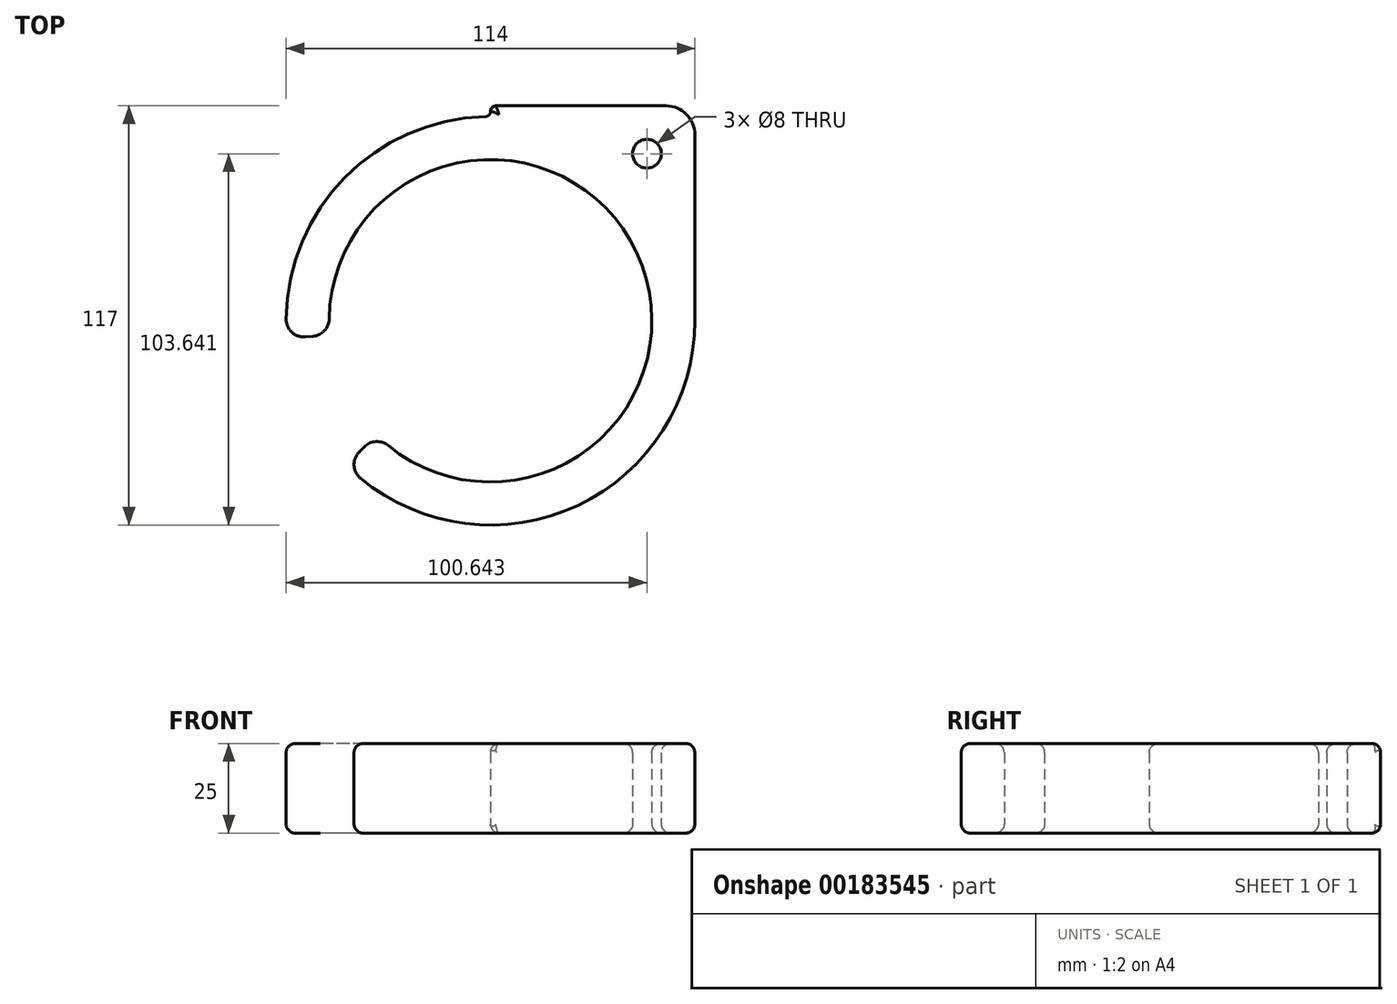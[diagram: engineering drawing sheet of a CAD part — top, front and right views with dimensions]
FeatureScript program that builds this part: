
annotation { "Feature Type Name" : "Feature", "Feature Type Description" : "" }
export const myFeature = defineFeature(function(context is Context, id is Id, definition is map)
    precondition{}
    {
        {
            var Q0;
            Q0=qCreatedBy(makeId("Top.planeOp"),FACE);
            var sketch = newSketch(context, id + "F0", { "sketchPlane" : qUnion([Q0])});
            skCircle(sketch, "E0", {"center": v(-22.2, -19.05) * mm, "radius": 45 * mm});
            skCircle(sketch, "E1", {"center": v(-22.2, -19.05) * mm, "radius": 57 * mm});
            skLineSegment(sketch, "E2.bottom", {"start": v(-22.2, -19.05) * mm, "end": v(34.8, -19.05) * mm});
            skLineSegment(sketch, "E2.top", {"start": v(-22.2, 40.95) * mm, "end": v(34.8, 40.95) * mm});
            skLineSegment(sketch, "E2.left", {"start": v(-22.2, -19.05) * mm, "end": v(-22.2, 40.95) * mm});
            skLineSegment(sketch, "E2.right", {"start": v(34.8, -19.05) * mm, "end": v(34.8, 40.95) * mm});
            skLineSegment(sketch, "E3", {"start": v(34.8, 40.95) * mm, "end": v(8.08, 14.23) * mm, "construction": true});
            skCircle(sketch, "E4", {"center": v(21.43, 27.6) * mm, "radius": 4 * mm});
            skLineSegment(sketch, "E5", {"start": v(-22.2, -19.05) * mm, "end": v(-79, -24.02) * mm});
            skLineSegment(sketch, "E6", {"start": v(-22.2, -19.05) * mm, "end": v(-62.51, -59.36) * mm});
            skSolve(sketch);
        }
        {
            var Q0;
            {var subQ0=sQuery(id+"F0.wireOp",EDGE,"E2.left");var subQ1=sQuery(id+"F0.wireOp",EDGE,"E0");var subQ2=makeQuery(id+"F0.imprint","INTERSECT",VERTEX,{"derivedFrom":[subQ1,subQ0]});Q0=makeQuery(id+"F0.imprint","IMPRINT",FACE,{"disambiguationData":[TD([[makeQuery(id+"F0.imprint","IMPRINT",EDGE,{"disambiguationData":[TD([[subQ2,1.0]])],"derivedFrom":subQ1}),-1.0]])]});}
            var Q1;
            {var subQ2=sQuery(id+"F0.wireOp",EDGE,"E2.top");Q1=makeQuery(id+"F0.imprint","IMPRINT",FACE,{"disambiguationData":[TD([[makeQuery(id+"F0.imprint","IMPRINT",EDGE,{"derivedFrom":subQ2}),-1.0]])]});}
            var Q2;
            {var subQ0=sQuery(id+"F0.wireOp",EDGE,"E2.left");var subQ1=sQuery(id+"F0.wireOp",EDGE,"E0");var subQ2=makeQuery(id+"F0.imprint","INTERSECT",VERTEX,{"derivedFrom":[subQ1,subQ0]});Q2=makeQuery(id+"F0.imprint","IMPRINT",FACE,{"disambiguationData":[TD([[makeQuery(id+"F0.imprint","IMPRINT",EDGE,{"disambiguationData":[TD([[subQ2,-1.0]])],"derivedFrom":subQ1}),-1.0]])]});}
            var Q3;
            {var subQ0=sQuery(id+"F0.wireOp",EDGE,"E2.bottom");var subQ1=sQuery(id+"F0.wireOp",EDGE,"E0");var subQ2=makeQuery(id+"F0.imprint","INTERSECT",VERTEX,{"derivedFrom":[subQ1,subQ0]});Q3=makeQuery(id+"F0.imprint","IMPRINT",FACE,{"disambiguationData":[TD([[makeQuery(id+"F0.imprint","IMPRINT",EDGE,{"disambiguationData":[TD([[subQ2,1.0]])],"derivedFrom":subQ1}),-1.0]])]});}
            extrude(context, id + "F1", {"entities" : qUnion([Q0, Q1, Q2, Q3]), "depth" : 25 * mm});
        }
        {
            var Q0;
            Q0=makeQuery(id+"F1.opExtrude","SWEPT_EDGE",EDGE,{"disambiguationData":[OSD([sQuery(id+"F0.wireOp",EDGE,"E2.top"),sQuery(id+"F0.wireOp",EDGE,"E2.left")])]});
            var Q1;
            Q1=makeQuery(id+"F1.opExtrude","SWEPT_EDGE",EDGE,{"disambiguationData":[OSD([sQuery(id+"F0.wireOp",EDGE,"E1"),sQuery(id+"F0.wireOp",EDGE,"E2.left")])]});
            fillet(context, id + "F2", {"entities" : qUnion([Q0, Q1]), "radius" : 1.5 * mm, "tangentPropagation" : true, "allowEdgeOverflow" : false});
        }
        {
            var Q0;
            Q0=makeQuery(id+"F1.opExtrude","SWEPT_EDGE",EDGE,{"disambiguationData":[OSD([sQuery(id+"F0.wireOp",EDGE,"E0"),sQuery(id+"F0.wireOp",EDGE,"E5")])]});
            var Q1;
            Q1=makeQuery(id+"F1.opExtrude","SWEPT_EDGE",EDGE,{"disambiguationData":[OSD([sQuery(id+"F0.wireOp",EDGE,"E0"),sQuery(id+"F0.wireOp",EDGE,"E6")])]});
            var Q2;
            Q2=makeQuery(id+"F1.opExtrude","SWEPT_EDGE",EDGE,{"disambiguationData":[OSD([sQuery(id+"F0.wireOp",EDGE,"E1"),sQuery(id+"F0.wireOp",EDGE,"E6")])]});
            var Q3;
            Q3=makeQuery(id+"F1.opExtrude","SWEPT_EDGE",EDGE,{"disambiguationData":[OSD([sQuery(id+"F0.wireOp",EDGE,"E1"),sQuery(id+"F0.wireOp",EDGE,"E5")])]});
            fillet(context, id + "F3", {"entities" : qUnion([Q0, Q1, Q2, Q3]), "radius" : 5 * mm, "tangentPropagation" : true, "allowEdgeOverflow" : false});
        }
        {
            var Q0;
            Q0=makeQuery(id+"F1.opExtrude","SWEPT_EDGE",EDGE,{"disambiguationData":[OSD([sQuery(id+"F0.wireOp",EDGE,"E2.top"),sQuery(id+"F0.wireOp",EDGE,"E2.right")])]});
            fillet(context, id + "F4", {"entities" : qUnion([Q0]), "radius" : 8 * mm, "tangentPropagation" : true, "allowEdgeOverflow" : false});
        }
        {
            var Q0;
            Q0=makeQuery(id+"F1.opExtrude","CAP_EDGE",EDGE,{"disambiguationData":[OSD([sQuery(id+"F0.wireOp",EDGE,"E0")])],"isStart":true});
            var Q1;
            {var subQ0=sQuery(id+"F0.wireOp",EDGE,"E5");var subQ1=sQuery(id+"F0.wireOp",EDGE,"E0");Q1=makeQuery(id+"F3.opFillet","BLEND_EDGE",EDGE,{"blendedFrom":[makeQuery(id+"F1.opExtrude","SWEPT_EDGE",EDGE,{"disambiguationData":[OSD([subQ1,subQ0])]}),makeQuery(id+"F1.opExtrude","CAP_FACE",FACE,{"disambiguationData":[OSD([subQ1,sQuery(id+"F0.wireOp",EDGE,"E1"),sQuery(id+"F0.wireOp",EDGE,"E2.top"),sQuery(id+"F0.wireOp",EDGE,"E2.left"),sQuery(id+"F0.wireOp",EDGE,"E2.right"),sQuery(id+"F0.wireOp",EDGE,"E4"),subQ0,sQuery(id+"F0.wireOp",EDGE,"E6")])],"isStart":true})],"blendedInto":[makeQuery(id+"F1.opExtrude","CAP_FACE",FACE,{"disambiguationData":[OSD([subQ1,sQuery(id+"F0.wireOp",EDGE,"E1"),sQuery(id+"F0.wireOp",EDGE,"E2.top"),sQuery(id+"F0.wireOp",EDGE,"E2.left"),sQuery(id+"F0.wireOp",EDGE,"E2.right"),sQuery(id+"F0.wireOp",EDGE,"E4"),subQ0,sQuery(id+"F0.wireOp",EDGE,"E6")])],"isStart":true})]});}
            var Q2;
            Q2=makeQuery(id+"F1.opExtrude","CAP_FACE",FACE,{"disambiguationData":[OSD([sQuery(id+"F0.wireOp",EDGE,"E0"),sQuery(id+"F0.wireOp",EDGE,"E1"),sQuery(id+"F0.wireOp",EDGE,"E2.top"),sQuery(id+"F0.wireOp",EDGE,"E2.left"),sQuery(id+"F0.wireOp",EDGE,"E2.right"),sQuery(id+"F0.wireOp",EDGE,"E4"),sQuery(id+"F0.wireOp",EDGE,"E5"),sQuery(id+"F0.wireOp",EDGE,"E6")])],"isStart":true});
            var Q3;
            Q3=makeQuery(id+"F1.opExtrude","CAP_FACE",FACE,{"disambiguationData":[OSD([sQuery(id+"F0.wireOp",EDGE,"E0"),sQuery(id+"F0.wireOp",EDGE,"E1"),sQuery(id+"F0.wireOp",EDGE,"E2.top"),sQuery(id+"F0.wireOp",EDGE,"E2.left"),sQuery(id+"F0.wireOp",EDGE,"E2.right"),sQuery(id+"F0.wireOp",EDGE,"E4"),sQuery(id+"F0.wireOp",EDGE,"E5"),sQuery(id+"F0.wireOp",EDGE,"E6")])],"isStart":false});
            fillet(context, id + "F5", {"entities" : qUnion([Q0, Q1, Q2, Q3]), "radius" : 2.5 * mm, "tangentPropagation" : true, "allowEdgeOverflow" : false});
        }
    });
